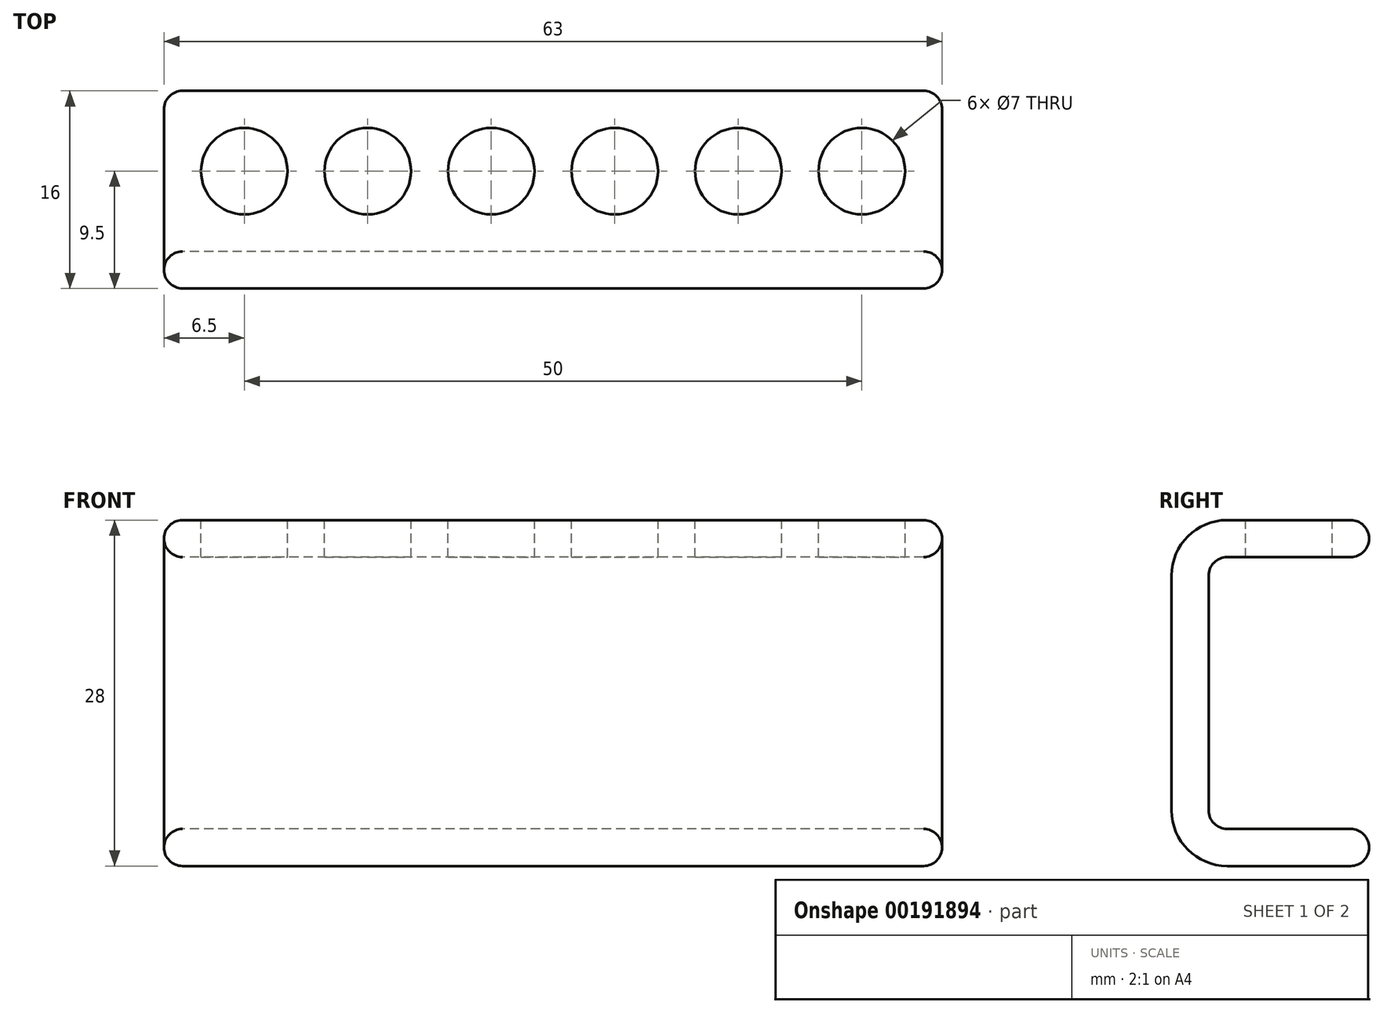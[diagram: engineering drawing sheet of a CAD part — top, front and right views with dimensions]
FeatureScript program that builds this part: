
annotation { "Feature Type Name" : "Feature", "Feature Type Description" : "" }
export const myFeature = defineFeature(function(context is Context, id is Id, definition is map)
    precondition{}
    {
        {
            assignVariable(context, id + "F0", {"name" : "Interval", "anyValue" : 3});
        }
        {
            assignVariable(context, id + "F1", {"name" : "thickness", "anyValue" : 3});
        }
        {
            assignVariable(context, id + "F2", {"name" : "diameter", "anyValue" : 7});
        }
        {
            assignVariable(context, id + "F3", {"name" : "numCircles", "anyValue" : 6});
        }
        {
            var Q0;
            Q0=qCreatedBy(makeId("Right.planeOp"),FACE);
            var sketch = newSketch(context, id + "F4", { "sketchPlane" : qUnion([Q0])});
            skLineSegment(sketch, "E0", {"start": v(0, 0) * mm, "end": v(0, 14) * mm});
            skLineSegment(sketch, "E1", {"start": v(0, 14) * mm, "end": v(16, 14) * mm});
            skLineSegment(sketch, "E2", {"start": v(16, 14) * mm, "end": v(16, 11) * mm});
            skLineSegment(sketch, "E3", {"start": v(16, 11) * mm, "end": v(3, 11) * mm});
            skLineSegment(sketch, "E4", {"start": v(3, 11) * mm, "end": v(3, 0) * mm});
            skLineSegment(sketch, "E5", {"start": v(0, 0) * mm, "end": v(3, 0) * mm, "construction": true});
            skLineSegment(sketch, "E6.MirrorCS", {"start": v(0, 0) * mm, "end": v(0, -14) * mm});
            skLineSegment(sketch, "E7.MirrorCS", {"start": v(0, -14) * mm, "end": v(16, -14) * mm});
            skLineSegment(sketch, "E8.MirrorCS", {"start": v(16, -11) * mm, "end": v(3, -11) * mm});
            skLineSegment(sketch, "E9.MirrorCS", {"start": v(3, -11) * mm, "end": v(3, 0) * mm});
            skLineSegment(sketch, "E10.MirrorCS", {"start": v(16, -14) * mm, "end": v(16, -11) * mm});
            skSolve(sketch);
        }
        {
            var Q0;
            Q0=makeQuery(id+"F4.imprint","IMPRINT",FACE,{"disambiguationData":[TD([[makeQuery(id+"F4.imprint","IMPRINT",EDGE,{"derivedFrom":sQuery(id+"F4.wireOp",EDGE,"E0")}),-1.0]])]});
            extrude(context, id + "F5", {"entities" : qUnion([Q0]), "endBound" : BoundingType.SYMMETRIC, "depth" : (getVariable(context, 'diameter') * getVariable(context, 'numCircles') + getVariable(context, 'thickness') * (getVariable(context, 'numCircles') + 1)) * mm});
        }
        {
            var Q0;
            Q0=makeQuery(id+"F5.opExtrude","SWEPT_FACE",FACE,{"disambiguationData":[OSD([sQuery(id+"F4.wireOp",EDGE,"E1")])]});
            var sketch = newSketch(context, id + "F6", { "sketchPlane" : qUnion([Q0])});
            skLineSegment(sketch, "E11", {"start": v(-31.5, 3) * mm, "end": v(31.5, 3) * mm, "construction": true});
            skCircle(sketch, "E12", {"center": v(-25, 9.5) * mm, "radius": 3.5 * mm});
            skLineSegment(sketch, "E13", {"start": v(-25, 3) * mm, "end": v(-25, 16) * mm, "construction": true});
            skLineSegment(sketch, "E14", {"start": v(-28.5, 9.5) * mm, "end": v(-31.5, 9.5) * mm, "construction": true});
            skCircle(sketch, "E15.1.0.0", {"center": v(-15, 9.5) * mm, "radius": 3.5 * mm});
            skCircle(sketch, "E15.2.0.0", {"center": v(-5, 9.5) * mm, "radius": 3.5 * mm});
            skCircle(sketch, "E15.3.0.0", {"center": v(5, 9.5) * mm, "radius": 3.5 * mm});
            skCircle(sketch, "E15.4.0.0", {"center": v(15, 9.5) * mm, "radius": 3.5 * mm});
            skCircle(sketch, "E15.5.0.0", {"center": v(25, 9.5) * mm, "radius": 3.5 * mm});
            skLineSegment(sketch, "E15.direction1", {"start": v(-25, 9.5) * mm, "end": v(-15, 9.5) * mm, "construction": true});
            skLineSegment(sketch, "E16", {"start": v(28.5, 9.5) * mm, "end": v(31.5, 9.5) * mm, "construction": true});
            skLineSegment(sketch, "E17", {"start": v(18.5, 9.5) * mm, "end": v(21.5, 9.5) * mm, "construction": true});
            skSolve(sketch);
        }
        {
            var Q0;
            Q0 = qSketchRegion(id + "F6", true);
            extrude(context, id + "F7", {"entities" : qUnion([Q0]), "operationType" : NewBodyOperationType.REMOVE, "endBound" : BoundingType.UP_TO_NEXT, "oppositeDirection" : true, "depth" : 25 * mm});
        }
        {
            var Q0;
            Q0=makeQuery(id+"F5.opExtrude","SWEPT_FACE",FACE,{"disambiguationData":[OSD([sQuery(id+"F4.wireOp",EDGE,"E2")])]});
            var Q1;
            Q1=makeQuery(id+"F5.opExtrude","SWEPT_FACE",FACE,{"disambiguationData":[OSD([sQuery(id+"F4.wireOp",EDGE,"E10.MirrorCS")])]});
            var Q2;
            Q2=makeQuery(id+"F5.opExtrude","SWEPT_EDGE",EDGE,{"disambiguationData":[OSD([sQuery(id+"F4.wireOp",EDGE,"E8.MirrorCS"),sQuery(id+"F4.wireOp",EDGE,"E9.MirrorCS")])]});
            var Q3;
            Q3=makeQuery(id+"F5.opExtrude","SWEPT_EDGE",EDGE,{"disambiguationData":[OSD([sQuery(id+"F4.wireOp",EDGE,"E3"),sQuery(id+"F4.wireOp",EDGE,"E4")])]});
            var Q4;
            Q4=makeQuery(id+"F5.opExtrude","CAP_FACE",FACE,{"disambiguationData":[OSD([sQuery(id+"F4.wireOp",EDGE,"E0"),sQuery(id+"F4.wireOp",EDGE,"E1"),sQuery(id+"F4.wireOp",EDGE,"E2"),sQuery(id+"F4.wireOp",EDGE,"E3"),sQuery(id+"F4.wireOp",EDGE,"E4"),sQuery(id+"F4.wireOp",EDGE,"E6.MirrorCS"),sQuery(id+"F4.wireOp",EDGE,"E7.MirrorCS"),sQuery(id+"F4.wireOp",EDGE,"E8.MirrorCS"),sQuery(id+"F4.wireOp",EDGE,"E9.MirrorCS"),sQuery(id+"F4.wireOp",EDGE,"E10.MirrorCS")])],"isStart":false});
            var Q5;
            Q5=makeQuery(id+"F5.opExtrude","CAP_FACE",FACE,{"disambiguationData":[OSD([sQuery(id+"F4.wireOp",EDGE,"E0"),sQuery(id+"F4.wireOp",EDGE,"E1"),sQuery(id+"F4.wireOp",EDGE,"E2"),sQuery(id+"F4.wireOp",EDGE,"E3"),sQuery(id+"F4.wireOp",EDGE,"E4"),sQuery(id+"F4.wireOp",EDGE,"E6.MirrorCS"),sQuery(id+"F4.wireOp",EDGE,"E7.MirrorCS"),sQuery(id+"F4.wireOp",EDGE,"E8.MirrorCS"),sQuery(id+"F4.wireOp",EDGE,"E9.MirrorCS"),sQuery(id+"F4.wireOp",EDGE,"E10.MirrorCS")])],"isStart":true});
            fillet(context, id + "F8", {"entities" : qUnion([Q0, Q1, Q2, Q3, Q4, Q5]), "radius" : (getVariable(context, 'Interval') / 2) * mm, "tangentPropagation" : true, "allowEdgeOverflow" : false});
        }
        {
            var Q0;
            Q0=makeQuery(id+"F5.opExtrude","SWEPT_EDGE",EDGE,{"disambiguationData":[OSD([sQuery(id+"F4.wireOp",EDGE,"E0"),sQuery(id+"F4.wireOp",EDGE,"E1")])]});
            var Q1;
            Q1=makeQuery(id+"F5.opExtrude","SWEPT_EDGE",EDGE,{"disambiguationData":[OSD([sQuery(id+"F4.wireOp",EDGE,"E6.MirrorCS"),sQuery(id+"F4.wireOp",EDGE,"E7.MirrorCS")])]});
            fillet(context, id + "F9", {"entities" : qUnion([Q0, Q1]), "radius" : (3 * getVariable(context, 'thickness') / 2) * mm, "tangentPropagation" : true, "allowEdgeOverflow" : false});
        }
    });
